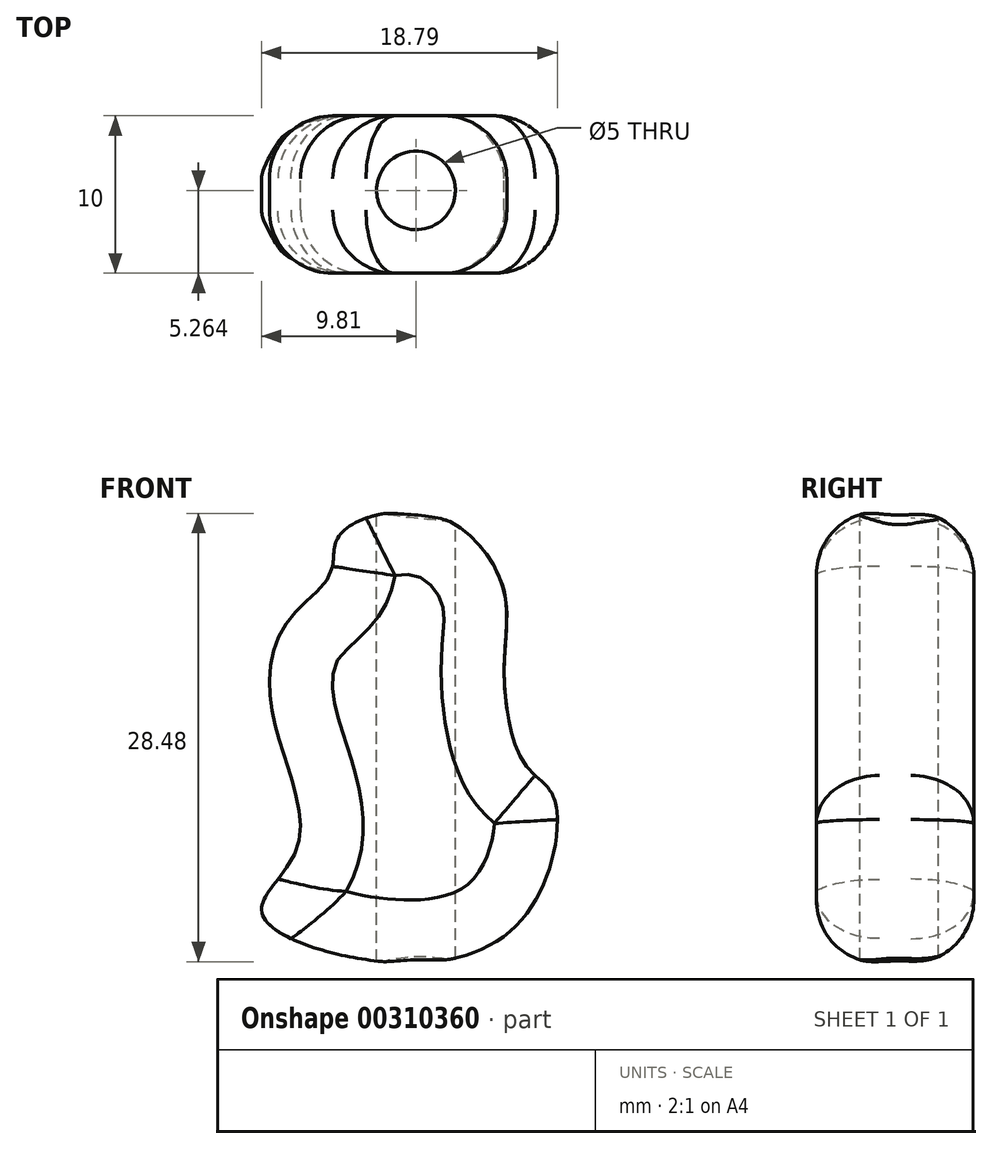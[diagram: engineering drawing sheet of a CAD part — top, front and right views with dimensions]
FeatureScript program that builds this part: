
annotation { "Feature Type Name" : "Feature", "Feature Type Description" : "" }
export const myFeature = defineFeature(function(context is Context, id is Id, definition is map)
    precondition{}
    {
        {
            var Q0;
            Q0=qCreatedBy(makeId("Front.planeOp"),FACE);
            var sketch = newSketch(context, id + "F0", { "sketchPlane" : qUnion([Q0])});
            skPoint(sketch, "E0.9.internal.snap0", {"position": v(5, 11.21) * mm});
            skFitSpline(sketch, "E0", {"points": [v(-1.93, 4.4) * mm, v(0.85, 7.52) * mm, v(1.38, 9.9) * mm, v(7.35, 11.21) * mm, v(11.8, 6.6) * mm, v(11.86, 1.75) * mm, v(13.12, -4.55) * mm, v(15, -6.74) * mm, v(13.39, -13.97) * mm, v(5, -17.22) * mm, v(-3.52, -14.04) * mm, v(-1.27, -9.86) * mm, v(-2.8, -1.7) * mm, v(-1.93, 4.4) * mm]});
            skPoint(sketch, "E1.orphan", {"position": v(15, 11.21) * mm});
            skPoint(sketch, "E2.left.start.orphan", {"position": v(-5, 11.21) * mm});
            skSolve(sketch);
        }
        {
            var Q0;
            Q0=makeQuery(id+"F0.imprint","IMPRINT",FACE,{"disambiguationData":[TD([[makeQuery(id+"F0.imprint","IMPRINT",EDGE,{"derivedFrom":sQuery(id+"F0.wireOp",EDGE,"E0")}),-1.0]])]});
            extrude(context, id + "F1", {"entities" : qUnion([Q0]), "depth" : 10 * mm});
        }
        {
            var Q0;
            Q0=makeQuery(id+"F1.opExtrude","CAP_EDGE",EDGE,{"disambiguationData":[OSD([sQuery(id+"F0.wireOp",EDGE,"E0")])],"isStart":false});
            var Q1;
            Q1=makeQuery(id+"F1.opExtrude","CAP_EDGE",EDGE,{"disambiguationData":[OSD([sQuery(id+"F0.wireOp",EDGE,"E0")])],"isStart":true});
            fillet(context, id + "F2", {"entities" : qUnion([Q0, Q1]), "radius" : 4 * mm, "tangentPropagation" : true, "allowEdgeOverflow" : false});
        }
        {
            var Q0;
            Q0=qCreatedBy(makeId("Top.planeOp"),FACE);
            var sketch = newSketch(context, id + "F3", { "sketchPlane" : qUnion([Q0])});
            skCircle(sketch, "E3", {"center": v(6.26, -4.74) * mm, "radius": 2.5 * mm});
            skSolve(sketch);
        }
        {
            var Q0;
            Q0 = qSketchRegion(id + "F3", true);
            var Q1;
            Q1=sQuery(id+"F3.wireOp",EDGE,"E3");
            extrude(context, id + "F4", {"entities" : qUnion([Q0]), "operationType" : NewBodyOperationType.REMOVE, "surfaceEntities" : qUnion([Q1]), "endBound" : BoundingType.SYMMETRIC, "oppositeDirection" : true, "depth" : 52.6 * mm});
        }
    });
